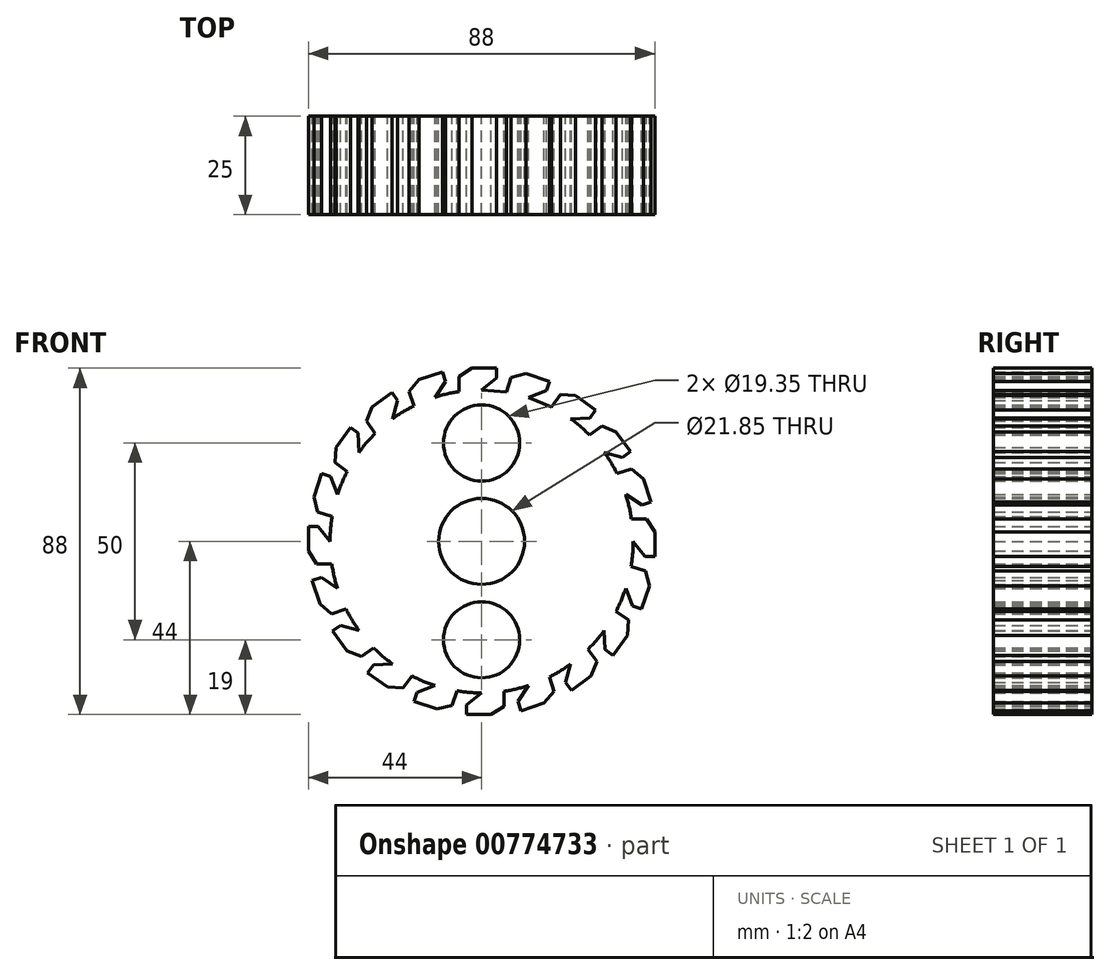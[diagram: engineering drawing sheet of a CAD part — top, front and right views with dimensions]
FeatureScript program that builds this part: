
annotation { "Feature Type Name" : "Feature", "Feature Type Description" : "" }
export const myFeature = defineFeature(function(context is Context, id is Id, definition is map)
    precondition{}
    {
        {
            var Q0;
            Q0=qCreatedBy(makeId("Front.planeOp"),FACE);
            var sketch = newSketch(context, id + "F0", { "sketchPlane" : qUnion([Q0])});
            skCircle(sketch, "E0", {"center": v(0, 0) * mm, "radius": 10.93 * mm});
            skLineSegment(sketch, "E1", {"start": v(0, 0) * mm, "end": v(0, 25) * mm, "construction": true});
            skCircle(sketch, "E2", {"center": v(0, 25) * mm, "radius": 9.68 * mm});
            skLineSegment(sketch, "E3", {"start": v(0, 0) * mm, "end": v(0, 44) * mm, "construction": true});
            skLineSegment(sketch, "E4", {"start": v(-2.43, 44) * mm, "end": v(3.8, 44) * mm});
            skLineSegment(sketch, "E5", {"start": v(3.8, 44) * mm, "end": v(3.8, 41.54) * mm});
            skLineSegment(sketch, "E6", {"start": v(3.8, 41.54) * mm, "end": v(0, 38.5) * mm});
            skLineSegment(sketch, "E7", {"start": v(-2.43, 44) * mm, "end": v(-5.74, 41.9) * mm});
            skLineSegment(sketch, "E8", {"start": v(-5.74, 41.9) * mm, "end": v(-5.74, 38.07) * mm});
            skLineSegment(sketch, "E9.1.0", {"start": v(-9.22, 40.69) * mm, "end": v(-11.9, 36.62) * mm});
            skLineSegment(sketch, "E9.1.1", {"start": v(-9.98, 43.02) * mm, "end": v(-9.22, 40.69) * mm});
            skLineSegment(sketch, "E9.1.2", {"start": v(-15.9, 41.1) * mm, "end": v(-9.98, 43.02) * mm});
            skLineSegment(sketch, "E9.1.3", {"start": v(-15.9, 41.1) * mm, "end": v(-18.4, 38.09) * mm});
            skLineSegment(sketch, "E9.1.4", {"start": v(-18.4, 38.09) * mm, "end": v(-17.22, 34.43) * mm});
            skLineSegment(sketch, "E9.2.0", {"start": v(-21.34, 35.85) * mm, "end": v(-22.63, 31.15) * mm});
            skLineSegment(sketch, "E9.2.1", {"start": v(-22.78, 37.83) * mm, "end": v(-21.34, 35.85) * mm});
            skLineSegment(sketch, "E9.2.2", {"start": v(-27.83, 34.17) * mm, "end": v(-22.78, 37.83) * mm});
            skLineSegment(sketch, "E9.2.3", {"start": v(-27.83, 34.17) * mm, "end": v(-29.28, 30.53) * mm});
            skLineSegment(sketch, "E9.2.4", {"start": v(-29.28, 30.53) * mm, "end": v(-27.02, 27.43) * mm});
            skLineSegment(sketch, "E9.3.0", {"start": v(-31.37, 27.5) * mm, "end": v(-31.15, 22.63) * mm});
            skLineSegment(sketch, "E9.3.1", {"start": v(-33.36, 28.94) * mm, "end": v(-31.37, 27.5) * mm});
            skLineSegment(sketch, "E9.3.2", {"start": v(-37.02, 23.9) * mm, "end": v(-33.36, 28.94) * mm});
            skLineSegment(sketch, "E9.3.3", {"start": v(-37.02, 23.9) * mm, "end": v(-37.28, 20) * mm});
            skLineSegment(sketch, "E9.3.4", {"start": v(-37.28, 20) * mm, "end": v(-34.17, 17.74) * mm});
            skLineSegment(sketch, "E9.4.0", {"start": v(-38.33, 16.46) * mm, "end": v(-36.62, 11.9) * mm});
            skLineSegment(sketch, "E9.4.1", {"start": v(-40.67, 17.22) * mm, "end": v(-38.33, 16.46) * mm});
            skLineSegment(sketch, "E9.4.2", {"start": v(-42.6, 11.29) * mm, "end": v(-40.67, 17.22) * mm});
            skLineSegment(sketch, "E9.4.3", {"start": v(-42.6, 11.29) * mm, "end": v(-41.63, 7.5) * mm});
            skLineSegment(sketch, "E9.4.4", {"start": v(-41.63, 7.5) * mm, "end": v(-37.98, 6.3) * mm});
            skLineSegment(sketch, "E9.5.0", {"start": v(-41.54, 3.8) * mm, "end": v(-38.5, 0) * mm});
            skLineSegment(sketch, "E9.5.1", {"start": v(-44, 3.8) * mm, "end": v(-41.54, 3.8) * mm});
            skLineSegment(sketch, "E9.5.2", {"start": v(-44, -2.43) * mm, "end": v(-44, 3.8) * mm});
            skLineSegment(sketch, "E9.5.3", {"start": v(-44, -2.43) * mm, "end": v(-41.9, -5.74) * mm});
            skLineSegment(sketch, "E9.5.4", {"start": v(-41.9, -5.74) * mm, "end": v(-38.07, -5.74) * mm});
            skLineSegment(sketch, "E9.6.0", {"start": v(-40.69, -9.22) * mm, "end": v(-36.62, -11.9) * mm});
            skLineSegment(sketch, "E9.6.1", {"start": v(-43.02, -9.98) * mm, "end": v(-40.69, -9.22) * mm});
            skLineSegment(sketch, "E9.6.2", {"start": v(-41.1, -15.9) * mm, "end": v(-43.02, -9.98) * mm});
            skLineSegment(sketch, "E9.6.3", {"start": v(-41.1, -15.9) * mm, "end": v(-38.09, -18.4) * mm});
            skLineSegment(sketch, "E9.6.4", {"start": v(-38.09, -18.4) * mm, "end": v(-34.43, -17.22) * mm});
            skLineSegment(sketch, "E9.7.0", {"start": v(-35.85, -21.34) * mm, "end": v(-31.15, -22.63) * mm});
            skLineSegment(sketch, "E9.7.1", {"start": v(-37.83, -22.78) * mm, "end": v(-35.85, -21.34) * mm});
            skLineSegment(sketch, "E9.7.2", {"start": v(-34.17, -27.83) * mm, "end": v(-37.83, -22.78) * mm});
            skLineSegment(sketch, "E9.7.3", {"start": v(-34.17, -27.83) * mm, "end": v(-30.53, -29.28) * mm});
            skLineSegment(sketch, "E9.7.4", {"start": v(-30.53, -29.28) * mm, "end": v(-27.43, -27.02) * mm});
            skLineSegment(sketch, "E9.8.0", {"start": v(-27.5, -31.37) * mm, "end": v(-22.63, -31.15) * mm});
            skLineSegment(sketch, "E9.8.1", {"start": v(-28.94, -33.36) * mm, "end": v(-27.5, -31.37) * mm});
            skLineSegment(sketch, "E9.8.2", {"start": v(-23.9, -37.02) * mm, "end": v(-28.94, -33.36) * mm});
            skLineSegment(sketch, "E9.8.3", {"start": v(-23.9, -37.02) * mm, "end": v(-20, -37.28) * mm});
            skLineSegment(sketch, "E9.8.4", {"start": v(-20, -37.28) * mm, "end": v(-17.74, -34.17) * mm});
            skLineSegment(sketch, "E9.9.0", {"start": v(-16.46, -38.33) * mm, "end": v(-11.9, -36.62) * mm});
            skLineSegment(sketch, "E9.9.1", {"start": v(-17.22, -40.67) * mm, "end": v(-16.46, -38.33) * mm});
            skLineSegment(sketch, "E9.9.2", {"start": v(-11.29, -42.6) * mm, "end": v(-17.22, -40.67) * mm});
            skLineSegment(sketch, "E9.9.3", {"start": v(-11.29, -42.6) * mm, "end": v(-7.5, -41.63) * mm});
            skLineSegment(sketch, "E9.9.4", {"start": v(-7.5, -41.63) * mm, "end": v(-6.3, -37.98) * mm});
            skLineSegment(sketch, "E9.10.0", {"start": v(-3.8, -41.54) * mm, "end": v(0, -38.5) * mm});
            skLineSegment(sketch, "E9.10.1", {"start": v(-3.8, -44) * mm, "end": v(-3.8, -41.54) * mm});
            skLineSegment(sketch, "E9.10.2", {"start": v(2.43, -44) * mm, "end": v(-3.8, -44) * mm});
            skLineSegment(sketch, "E9.10.3", {"start": v(2.43, -44) * mm, "end": v(5.74, -41.9) * mm});
            skLineSegment(sketch, "E9.10.4", {"start": v(5.74, -41.9) * mm, "end": v(5.74, -38.07) * mm});
            skLineSegment(sketch, "E9.11.0", {"start": v(9.22, -40.69) * mm, "end": v(11.9, -36.62) * mm});
            skLineSegment(sketch, "E9.11.1", {"start": v(9.98, -43.02) * mm, "end": v(9.22, -40.69) * mm});
            skLineSegment(sketch, "E9.11.2", {"start": v(15.9, -41.1) * mm, "end": v(9.98, -43.02) * mm});
            skLineSegment(sketch, "E9.11.3", {"start": v(15.9, -41.1) * mm, "end": v(18.4, -38.09) * mm});
            skLineSegment(sketch, "E9.11.4", {"start": v(18.4, -38.09) * mm, "end": v(17.22, -34.43) * mm});
            skLineSegment(sketch, "E9.12.0", {"start": v(21.34, -35.85) * mm, "end": v(22.63, -31.15) * mm});
            skLineSegment(sketch, "E9.12.1", {"start": v(22.78, -37.83) * mm, "end": v(21.34, -35.85) * mm});
            skLineSegment(sketch, "E9.12.2", {"start": v(27.83, -34.17) * mm, "end": v(22.78, -37.83) * mm});
            skLineSegment(sketch, "E9.12.3", {"start": v(27.83, -34.17) * mm, "end": v(29.28, -30.53) * mm});
            skLineSegment(sketch, "E9.12.4", {"start": v(29.28, -30.53) * mm, "end": v(27.02, -27.43) * mm});
            skLineSegment(sketch, "E9.13.0", {"start": v(31.37, -27.5) * mm, "end": v(31.15, -22.63) * mm});
            skLineSegment(sketch, "E9.13.1", {"start": v(33.36, -28.94) * mm, "end": v(31.37, -27.5) * mm});
            skLineSegment(sketch, "E9.13.2", {"start": v(37.02, -23.9) * mm, "end": v(33.36, -28.94) * mm});
            skLineSegment(sketch, "E9.13.3", {"start": v(37.02, -23.9) * mm, "end": v(37.28, -20) * mm});
            skLineSegment(sketch, "E9.13.4", {"start": v(37.28, -20) * mm, "end": v(34.17, -17.74) * mm});
            skLineSegment(sketch, "E9.14.0", {"start": v(38.33, -16.46) * mm, "end": v(36.62, -11.9) * mm});
            skLineSegment(sketch, "E9.14.1", {"start": v(40.67, -17.22) * mm, "end": v(38.33, -16.46) * mm});
            skLineSegment(sketch, "E9.14.2", {"start": v(42.6, -11.29) * mm, "end": v(40.67, -17.22) * mm});
            skLineSegment(sketch, "E9.14.3", {"start": v(42.6, -11.29) * mm, "end": v(41.63, -7.5) * mm});
            skLineSegment(sketch, "E9.14.4", {"start": v(41.63, -7.5) * mm, "end": v(37.98, -6.3) * mm});
            skLineSegment(sketch, "E9.15.0", {"start": v(41.54, -3.8) * mm, "end": v(38.5, 0) * mm});
            skLineSegment(sketch, "E9.15.1", {"start": v(44, -3.8) * mm, "end": v(41.54, -3.8) * mm});
            skLineSegment(sketch, "E9.15.2", {"start": v(44, 2.43) * mm, "end": v(44, -3.8) * mm});
            skLineSegment(sketch, "E9.15.3", {"start": v(44, 2.43) * mm, "end": v(41.9, 5.74) * mm});
            skLineSegment(sketch, "E9.15.4", {"start": v(41.9, 5.74) * mm, "end": v(38.07, 5.74) * mm});
            skLineSegment(sketch, "E9.16.0", {"start": v(40.69, 9.22) * mm, "end": v(36.62, 11.9) * mm});
            skLineSegment(sketch, "E9.16.1", {"start": v(43.02, 9.98) * mm, "end": v(40.69, 9.22) * mm});
            skLineSegment(sketch, "E9.16.2", {"start": v(41.1, 15.9) * mm, "end": v(43.02, 9.98) * mm});
            skLineSegment(sketch, "E9.16.3", {"start": v(41.1, 15.9) * mm, "end": v(38.09, 18.4) * mm});
            skLineSegment(sketch, "E9.16.4", {"start": v(38.09, 18.4) * mm, "end": v(34.43, 17.22) * mm});
            skLineSegment(sketch, "E9.17.0", {"start": v(35.85, 21.34) * mm, "end": v(31.15, 22.63) * mm});
            skLineSegment(sketch, "E9.17.1", {"start": v(37.83, 22.78) * mm, "end": v(35.85, 21.34) * mm});
            skLineSegment(sketch, "E9.17.2", {"start": v(34.17, 27.83) * mm, "end": v(37.83, 22.78) * mm});
            skLineSegment(sketch, "E9.17.3", {"start": v(34.17, 27.83) * mm, "end": v(30.53, 29.28) * mm});
            skLineSegment(sketch, "E9.17.4", {"start": v(30.53, 29.28) * mm, "end": v(27.43, 27.02) * mm});
            skLineSegment(sketch, "E9.18.0", {"start": v(27.5, 31.37) * mm, "end": v(22.63, 31.15) * mm});
            skLineSegment(sketch, "E9.18.1", {"start": v(28.94, 33.36) * mm, "end": v(27.5, 31.37) * mm});
            skLineSegment(sketch, "E9.18.2", {"start": v(23.9, 37.02) * mm, "end": v(28.94, 33.36) * mm});
            skLineSegment(sketch, "E9.18.3", {"start": v(23.9, 37.02) * mm, "end": v(20, 37.28) * mm});
            skLineSegment(sketch, "E9.18.4", {"start": v(20, 37.28) * mm, "end": v(17.74, 34.17) * mm});
            skLineSegment(sketch, "E9.19.0", {"start": v(16.46, 38.33) * mm, "end": v(11.9, 36.62) * mm});
            skLineSegment(sketch, "E9.19.1", {"start": v(17.22, 40.67) * mm, "end": v(16.46, 38.33) * mm});
            skLineSegment(sketch, "E9.19.2", {"start": v(11.29, 42.6) * mm, "end": v(17.22, 40.67) * mm});
            skLineSegment(sketch, "E9.19.3", {"start": v(11.29, 42.6) * mm, "end": v(7.5, 41.63) * mm});
            skLineSegment(sketch, "E9.19.4", {"start": v(7.5, 41.63) * mm, "end": v(6.3, 37.98) * mm});
            skArc(sketch, "E10.trimOffspring", {"start": v(27.43, 27.02) * mm, "mid": v(25.11, 29.18) * mm, "end": v(22.63, 31.15) * mm});
            skArc(sketch, "E11.trimOffspring", {"start": v(34.43, 17.22) * mm, "mid": v(32.9, 20) * mm, "end": v(31.15, 22.63) * mm});
            skArc(sketch, "E12.trimOffspring", {"start": v(38.07, 5.74) * mm, "mid": v(37.47, 8.85) * mm, "end": v(36.62, 11.9) * mm});
            skArc(sketch, "E13.trimOffspring", {"start": v(37.98, -6.3) * mm, "mid": v(38.37, -3.16) * mm, "end": v(38.5, 0) * mm});
            skArc(sketch, "E14.trimOffspring", {"start": v(34.17, -17.74) * mm, "mid": v(35.51, -14.87) * mm, "end": v(36.62, -11.9) * mm});
            skArc(sketch, "E15.trimOffspring", {"start": v(-5.74, 38.07) * mm, "mid": v(-8.85, 37.47) * mm, "end": v(-11.9, 36.62) * mm});
            skArc(sketch, "E16.trimOffspring", {"start": v(-17.22, 34.43) * mm, "mid": v(-20, 32.9) * mm, "end": v(-22.63, 31.15) * mm});
            skArc(sketch, "E17.trimOffspring", {"start": v(-27.02, 27.43) * mm, "mid": v(-29.18, 25.11) * mm, "end": v(-31.15, 22.63) * mm});
            skArc(sketch, "E18.trimOffspring", {"start": v(-34.17, 17.74) * mm, "mid": v(-35.51, 14.87) * mm, "end": v(-36.62, 11.9) * mm});
            skArc(sketch, "E19.trimOffspring", {"start": v(-37.98, 6.3) * mm, "mid": v(-38.37, 3.16) * mm, "end": v(-38.5, 0) * mm});
            skArc(sketch, "E20.trimOffspring", {"start": v(-38.07, -5.74) * mm, "mid": v(-37.47, -8.85) * mm, "end": v(-36.62, -11.9) * mm});
            skArc(sketch, "E21.trimOffspring", {"start": v(-34.43, -17.22) * mm, "mid": v(-32.9, -20) * mm, "end": v(-31.15, -22.63) * mm});
            skLineSegment(sketch, "E22", {"start": v(0, 38.5) * mm, "end": v(6.3, 37.98) * mm});
            skLineSegment(sketch, "E23", {"start": v(11.9, 36.62) * mm, "end": v(17.74, 34.17) * mm});
            skArc(sketch, "E24.trimOffspring", {"start": v(-27.43, -27.02) * mm, "mid": v(-25.11, -29.18) * mm, "end": v(-22.63, -31.15) * mm});
            skArc(sketch, "E25.trimOffspring", {"start": v(-17.74, -34.17) * mm, "mid": v(-14.87, -35.51) * mm, "end": v(-11.9, -36.62) * mm});
            skArc(sketch, "E26.trimOffspring", {"start": v(-6.3, -37.98) * mm, "mid": v(-3.16, -38.37) * mm, "end": v(0, -38.5) * mm});
            skArc(sketch, "E27.trimOffspring", {"start": v(5.74, -38.07) * mm, "mid": v(8.85, -37.47) * mm, "end": v(11.9, -36.62) * mm});
            skArc(sketch, "E28.trimOffspring", {"start": v(17.22, -34.43) * mm, "mid": v(20, -32.9) * mm, "end": v(22.63, -31.15) * mm});
            skArc(sketch, "E29.trimOffspring", {"start": v(27.02, -27.43) * mm, "mid": v(29.18, -25.11) * mm, "end": v(31.15, -22.63) * mm});
            skCircle(sketch, "E30.1.0", {"center": v(0, -25) * mm, "radius": 9.68 * mm});
            skSolve(sketch);
        }
        {
            var Q0;
            Q0=makeQuery(id+"F0.imprint","IMPRINT",FACE,{"disambiguationData":[TD([[makeQuery(id+"F0.imprint","IMPRINT",EDGE,{"derivedFrom":sQuery(id+"F0.wireOp",EDGE,"E0")}),-1.0]])]});
            extrude(context, id + "F1", {"entities" : qUnion([Q0]), "depth" : 25 * mm, "offsetDistance" : 25 * mm});
        }
    });
